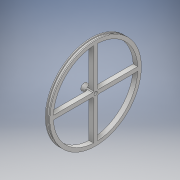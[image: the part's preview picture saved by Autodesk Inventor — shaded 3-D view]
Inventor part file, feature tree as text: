
AUTODESK INVENTOR PART (.ipt)
format: ipt  version: 2018 (Build 220112000, 112)  size: 198,656 bytes
history: native  units: mm
features: extrude x11, sketch x11, pattern_circular x1, fillet x1
ambient origin geometry x8: Origin, YZ Plane, XZ Plane, XY Plane, X Axis, Y Axis, Z Axis, Center Point
bodies: Solid1 (feature_tree)
feature tree (24):
  extrude  "Extrusion1"  Depth=3.5mm TaperAngle=0.0deg
  extrude  "Extrusion2"  Depth=1.0mm TaperAngle=0.0deg
  extrude  "Extrusion3"  Depth=1.0mm TaperAngle=0.0deg
  extrude  "Extrusion4"  Depth=6.0mm TaperAngle=0.0deg
  extrude  "Extrusion5"  Depth=10.0mm TaperAngle=0.0deg
  extrude  "Extrusion6"  Depth=1.0mm TaperAngle=0.0deg
  extrude  "Extrusion7"  Depth=1.0mm
  extrude  "Extrusion8"  Depth=4.0mm
  extrude  "Extrusion9"  Depth=40.0mm TaperAngle=360.0deg
  extrude  "Extrusion10"  Depth=2.0mm TaperAngle=0.0deg
  pattern_circular  "Circular Pattern1"  [2 undecoded]
  fillet  "Fillet1"  [1 undecoded]
  extrude  "Extrusion11"  [1 undecoded]
  sketch  "Sketch1"  dims[d0=88.0mm d1=3.5mm d2=0.0mm]
  sketch  "Sketch2"  dims[d3=90.0mm d4=1.0mm d5=0.0mm]
  sketch  "Sketch3"  dims[d6=90.0mm d7=1.0mm d8=0.0mm]
  sketch  "Sketch4"  dims[d9=83.0mm d10=6.0mm d11=0.0mm]
  sketch  "Sketch5"  dims[d12=7.0mm d13=10.0mm d14=0.0mm]
  sketch  "Sketch6"  dims[d15=2.0mm d16=0.0mm d17=1.0mm d18=0.0mm]
  sketch  "Sketch7"  dims[d19=1.0mm d20=0.0mm d21=3.25mm]
  sketch  "Sketch8"  dims[d22=10.0mm d23=0.0mm d24=4.0mm]
  sketch  "Sketch9"  dims[d25=4.5mm d26=0.0mm d27=40.0mm d28=360.0deg]
  sketch  "Sketch10"  dims[d30=2.0mm d31=2.0mm d32=0.0mm]
  sketch  "Sketch11"
note: 4 required parameter values undecoded (feature->parameter linkage not recoverable at this tier; creation-order binding heuristic only, values carry confidence <= 0.55)
